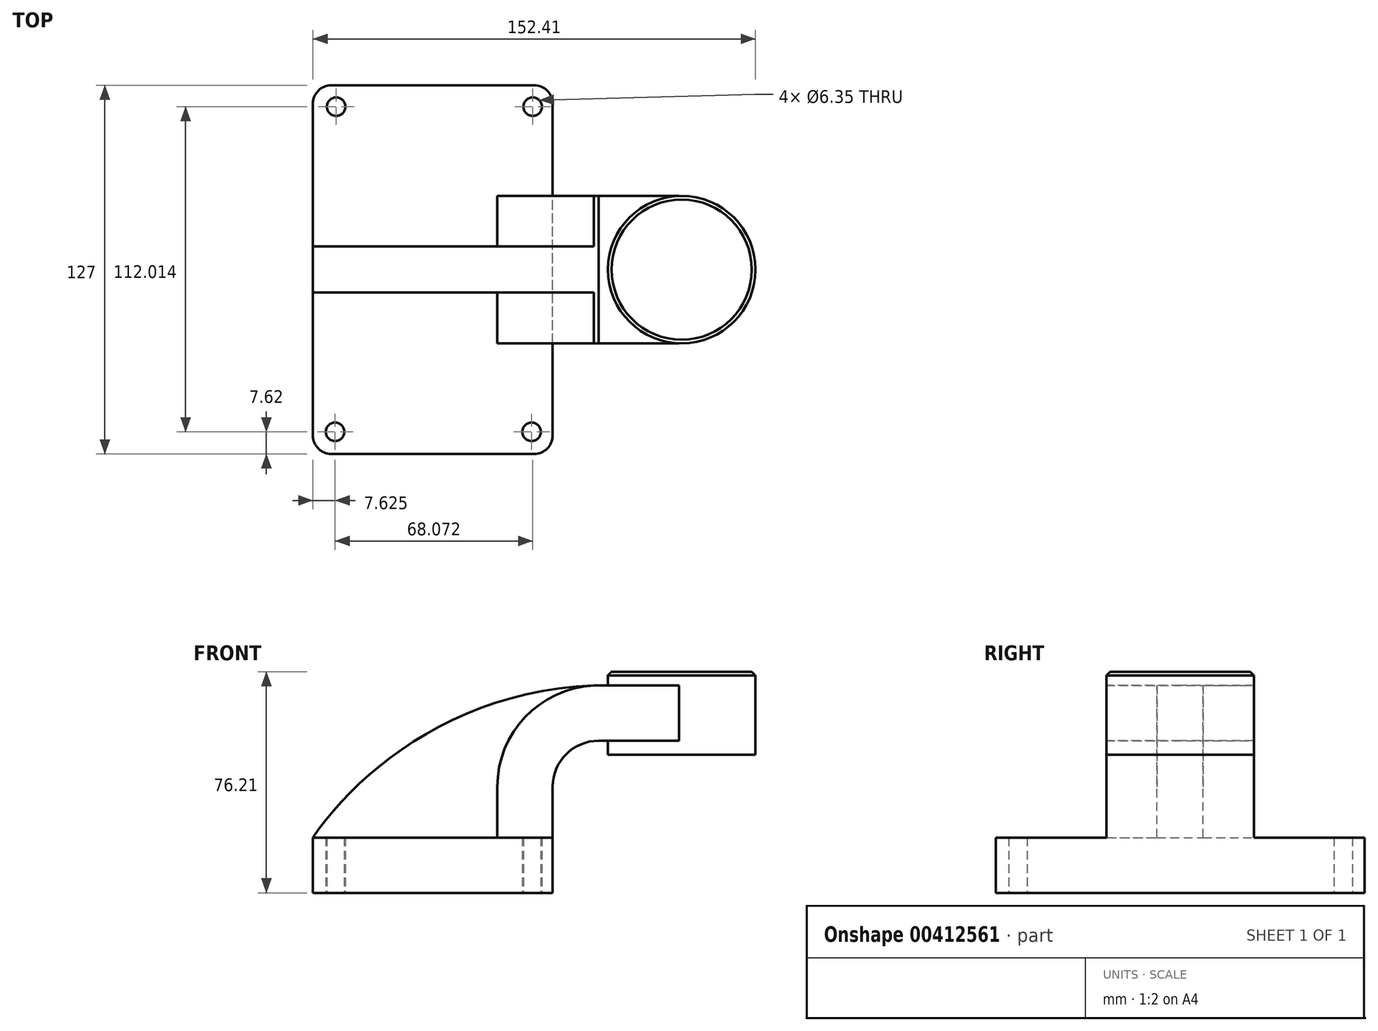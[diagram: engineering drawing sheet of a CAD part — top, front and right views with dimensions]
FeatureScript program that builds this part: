
annotation { "Feature Type Name" : "Feature", "Feature Type Description" : "" }
export const myFeature = defineFeature(function(context is Context, id is Id, definition is map)
    precondition{}
    {
        {
            var Q0;
            Q0=qCreatedBy(makeId("Front.planeOp"),FACE);
            var sketch = newSketch(context, id + "F0", { "sketchPlane" : qUnion([Q0])});
            skLineSegment(sketch, "E0.bottom", {"start": v(-41.28, -9.53) * mm, "end": v(41.28, -9.53) * mm});
            skLineSegment(sketch, "E0.top", {"start": v(-41.28, 9.53) * mm, "end": v(41.28, 9.53) * mm});
            skLineSegment(sketch, "E0.left", {"start": v(-41.28, -9.53) * mm, "end": v(-41.28, 9.53) * mm});
            skLineSegment(sketch, "E0.right", {"start": v(41.28, -9.53) * mm, "end": v(41.28, 9.53) * mm});
            skPoint(sketch, "E0.middle", {"position": v(0, 0) * mm});
            skLineSegment(sketch, "E1.bottom", {"start": v(60.32, 66.67) * mm, "end": v(111.12, 66.67) * mm});
            skLineSegment(sketch, "E1.top", {"start": v(60.33, 38.1) * mm, "end": v(111.12, 38.1) * mm});
            skLineSegment(sketch, "E1.left", {"start": v(60.32, 66.67) * mm, "end": v(60.33, 38.1) * mm});
            skLineSegment(sketch, "E1.right", {"start": v(111.12, 66.67) * mm, "end": v(111.12, 38.1) * mm});
            skPoint(sketch, "E1.middle", {"position": v(85.72, 52.39) * mm});
            skLineSegment(sketch, "E2", {"start": v(41.28, 9.53) * mm, "end": v(41.28, 27) * mm});
            skArc(sketch, "E3", {"start": v(41.28, 27) * mm, "mid": v(45.92, 38.23) * mm, "end": v(57.15, 42.88) * mm});
            skLineSegment(sketch, "E4", {"start": v(57.15, 42.88) * mm, "end": v(85.71, 42.88) * mm});
            skLineSegment(sketch, "E5.0", {"start": v(57.15, 61.93) * mm, "end": v(85.71, 61.93) * mm});
            skArc(sketch, "E5.1", {"start": v(22.23, 27) * mm, "mid": v(32.45, 51.7) * mm, "end": v(57.15, 61.93) * mm});
            skLineSegment(sketch, "E5.2", {"start": v(22.23, 9.53) * mm, "end": v(22.23, 27) * mm});
            skLineSegment(sketch, "E6", {"start": v(85.71, 38.1) * mm, "end": v(85.71, 66.67) * mm});
            skFitSpline(sketch, "E7", {"points": [v(-41.28, 9.53) * mm, v(57.15, 61.93) * mm], "startDerivative": vector(47.62, 70.77) * mm, "endDerivative": vector(142.34, 2.54) * mm});
            skSolve(sketch);
        }
        {
            var Q0;
            Q0=makeQuery(id+"F0.imprint","IMPRINT",FACE,{"disambiguationData":[TD([[makeQuery(id+"F0.imprint","IMPRINT",EDGE,{"derivedFrom":sQuery(id+"F0.wireOp",EDGE,"E0.bottom")}),1.0]])]});
            extrude(context, id + "F1", {"entities" : qUnion([Q0]), "endBound" : BoundingType.SYMMETRIC, "depth" : 127 * mm});
        }
        {
            var Q0;
            {var subQ0=sQuery(id+"F0.wireOp",EDGE,"E5.0");var subQ1=sQuery(id+"F0.wireOp",EDGE,"E1.left");var subQ2=makeQuery(id+"F0.imprint","INTERSECT",VERTEX,{"derivedFrom":[subQ1,subQ0]});Q0=makeQuery(id+"F0.imprint","IMPRINT",FACE,{"disambiguationData":[TD([[makeQuery(id+"F0.imprint","IMPRINT",EDGE,{"disambiguationData":[TD([[subQ2,-1.0]])],"derivedFrom":subQ1}),1.0]])]});}
            var Q1;
            {var subQ1=sQuery(id+"F0.wireOp",EDGE,"E2");Q1=makeQuery(id+"F0.imprint","IMPRINT",FACE,{"disambiguationData":[TD([[makeQuery(id+"F0.imprint","IMPRINT",EDGE,{"derivedFrom":subQ1}),1.0]])]});}
            extrude(context, id + "F2", {"entities" : qUnion([Q0, Q1]), "operationType" : NewBodyOperationType.ADD, "endBound" : BoundingType.SYMMETRIC, "depth" : 50.8 * mm});
        }
        {
            var Q0;
            {var subQ3=sQuery(id+"F0.wireOp",EDGE,"E5.2");Q0=makeQuery(id+"F0.imprint","IMPRINT",FACE,{"disambiguationData":[TD([[makeQuery(id+"F0.imprint","IMPRINT",EDGE,{"derivedFrom":subQ3}),1.0]])]});}
            extrude(context, id + "F3", {"entities" : qUnion([Q0]), "operationType" : NewBodyOperationType.ADD, "endBound" : BoundingType.SYMMETRIC, "depth" : 15.88 * mm});
        }
        {
            var Q0;
            {var subQ4=sQuery(id+"F0.wireOp",EDGE,"E1.right");Q0=makeQuery(id+"F0.imprint","IMPRINT",FACE,{"disambiguationData":[TD([[makeQuery(id+"F0.imprint","IMPRINT",EDGE,{"derivedFrom":subQ4}),-1.0]])]});}
            var Q1;
            Q1=sQuery(id+"F0.wireOp",EDGE,"E6");
            revolve(context, id + "F4", {"operationType" : NewBodyOperationType.ADD, "entities" : qUnion([Q0]), "axis" : qUnion([Q1]), "revolveType" : RevolveType.FULL});
        }
        {
            var Q0;
            Q0=makeQuery(id+"F1.opExtrude","CAP_EDGE",EDGE,{"disambiguationData":[OSD([sQuery(id+"F0.wireOp",EDGE,"E0.left")])],"isStart":false});
            var Q1;
            Q1=makeQuery(id+"F1.opExtrude","CAP_EDGE",EDGE,{"disambiguationData":[OSD([sQuery(id+"F0.wireOp",EDGE,"E0.right")])],"isStart":false});
            var Q2;
            Q2=makeQuery(id+"F1.opExtrude","CAP_EDGE",EDGE,{"disambiguationData":[OSD([sQuery(id+"F0.wireOp",EDGE,"E0.right")])],"isStart":true});
            var Q3;
            Q3=makeQuery(id+"F1.opExtrude","CAP_EDGE",EDGE,{"disambiguationData":[OSD([sQuery(id+"F0.wireOp",EDGE,"E0.left")])],"isStart":true});
            fillet(context, id + "F5", {"entities" : qUnion([Q0, Q1, Q2, Q3]), "radius" : 6.35 * mm, "tangentPropagation" : true, "allowEdgeOverflow" : false});
        }
        {
            var Q0;
            Q0=makeQuery(id+"F1.opExtrude","SWEPT_FACE",FACE,{"disambiguationData":[OSD([sQuery(id+"F0.wireOp",EDGE,"E0.bottom")])]});
            var sketch = newSketch(context, id + "F6", { "sketchPlane" : qUnion([Q0])});
            skCircle(sketch, "E8", {"center": v(-33.66, 55.88) * mm, "radius": 3.18 * mm});
            skCircle(sketch, "E9.1.0.0", {"center": v(34.04, 55.88) * mm, "radius": 3.18 * mm});
            skLineSegment(sketch, "E9.direction1", {"start": v(-33.66, 55.88) * mm, "end": v(34.04, 55.88) * mm, "construction": true});
            skCircle(sketch, "E10.1.0.0", {"center": v(34.42, -56.13) * mm, "radius": 3.18 * mm});
            skCircle(sketch, "E10.1.0.1", {"center": v(-33.27, -56.13) * mm, "radius": 3.18 * mm});
            skLineSegment(sketch, "E10.direction1", {"start": v(-33.66, 55.88) * mm, "end": v(-33.27, -56.13) * mm, "construction": true});
            skSolve(sketch);
        }
        {
            var Q0;
            Q0=sQuery(id+"F6.wireOp",VERTEX,"E8.center");
            var Q1;
            Q1=sQuery(id+"F6.wireOp",VERTEX,"E9.1.0.0.center");
            var Q2;
            Q2=sQuery(id+"F6.wireOp",VERTEX,"E10.1.0.0.center");
            var Q3;
            Q3=sQuery(id+"F6.wireOp",VERTEX,"E10.1.0.1.center");
            var Q4;
            Q4=makeQuery(id+"F1.opExtrude","SWEPT_BODY",BODY,{"disambiguationData":[OSD([sQuery(id+"F0.wireOp",EDGE,"E0.bottom"),sQuery(id+"F0.wireOp",EDGE,"E0.top"),sQuery(id+"F0.wireOp",EDGE,"E0.left"),sQuery(id+"F0.wireOp",EDGE,"E0.right")])]});
            hole(context, id + "F7", {"style" : HoleStyle.SIMPLE, "endStyle" : HoleEndStyle.THROUGH, "holeDiameter" : 6.35 * mm, "isTappedThrough" : true, "tappedDepth" : 12.7 * mm, "tapClearance" : 3, "locations" : qUnion([Q0, Q1, Q2, Q3]), "scope" : qUnion([Q4])});
        }
        {
            var Q0;
            Q0=makeQuery(id+"F4.opRevolve","SWEPT_EDGE",EDGE,{"disambiguationData":[OSD([sQuery(id+"F0.wireOp",EDGE,"E1.bottom"),sQuery(id+"F0.wireOp",EDGE,"E1.right")])]});
            chamfer(context, id + "F8", {"entities" : qUnion([Q0]), "chamferType" : ChamferType.OFFSET_ANGLE, "width" : 1.27 * mm, "oppositeDirection" : false, "angle" : 45 * degree, "tangentPropagation" : true});
        }
    });
